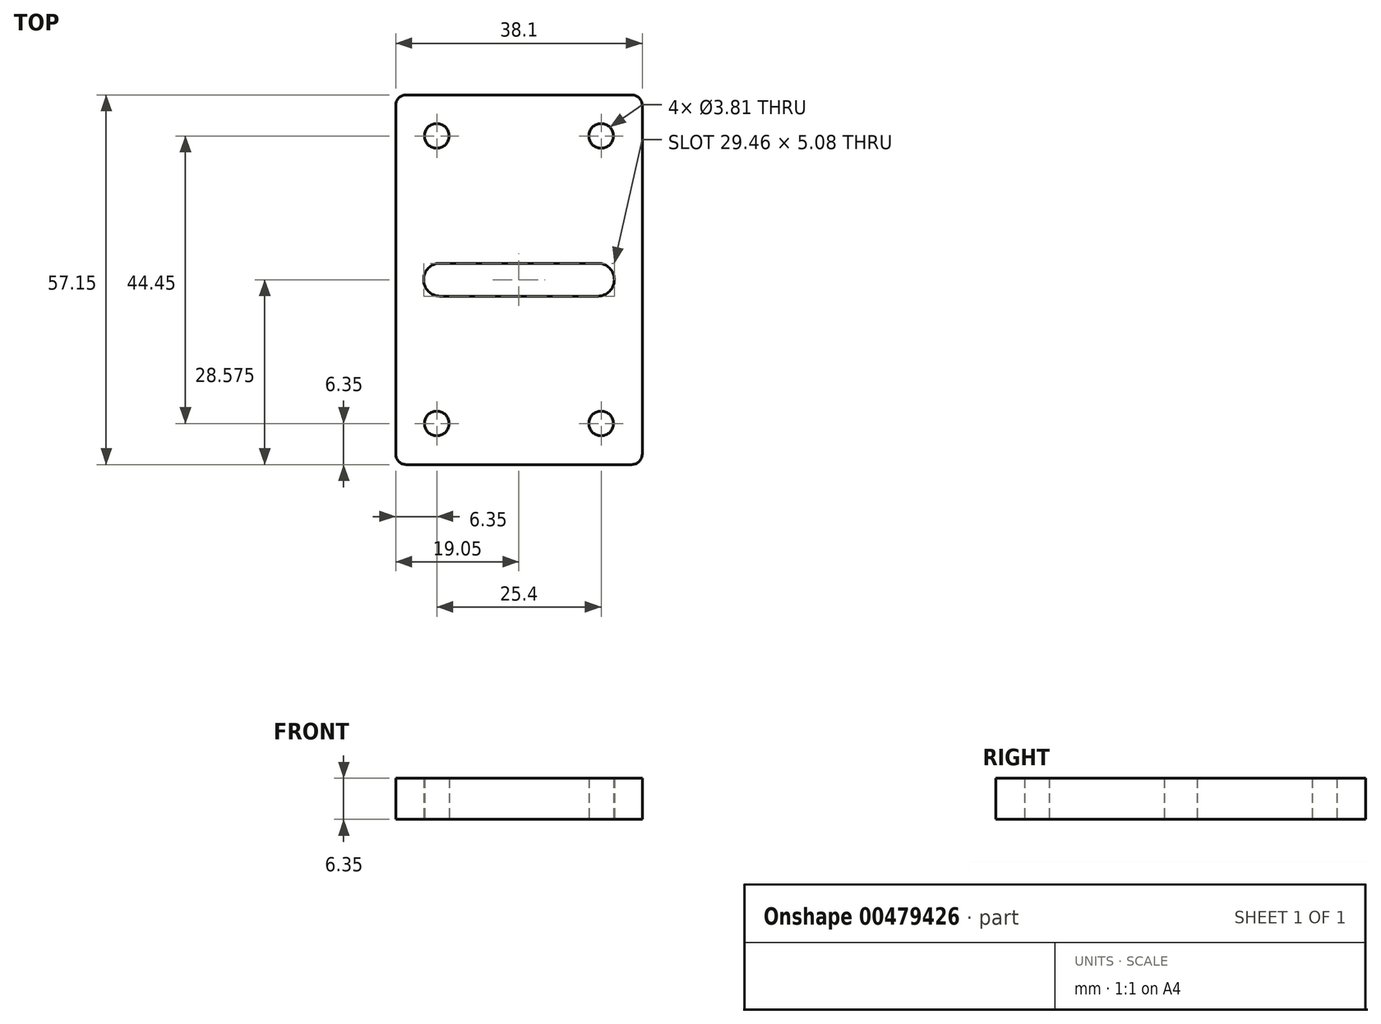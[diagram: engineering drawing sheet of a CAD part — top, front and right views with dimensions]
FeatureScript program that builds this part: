
annotation { "Feature Type Name" : "Feature", "Feature Type Description" : "" }
export const myFeature = defineFeature(function(context is Context, id is Id, definition is map)
    precondition{}
    {
        {
            var Q0;
            Q0=qCreatedBy(makeId("Top.planeOp"),FACE);
            var sketch = newSketch(context, id + "F0", { "sketchPlane" : qUnion([Q0])});
            skLineSegment(sketch, "E0.bottom", {"start": v(1.6, 0) * mm, "end": v(36.5, 0) * mm});
            skLineSegment(sketch, "E0.top", {"start": v(1.6, 57.15) * mm, "end": v(36.5, 57.15) * mm});
            skLineSegment(sketch, "E0.left", {"start": v(0, 1.6) * mm, "end": v(0, 55.55) * mm});
            skLineSegment(sketch, "E0.right", {"start": v(38.1, 1.6) * mm, "end": v(38.1, 55.55) * mm});
            skCircle(sketch, "E1", {"center": v(6.35, 50.8) * mm, "radius": 1.9 * mm});
            skCircle(sketch, "E2", {"center": v(31.75, 50.8) * mm, "radius": 1.9 * mm});
            skCircle(sketch, "E3", {"center": v(6.35, 6.35) * mm, "radius": 1.9 * mm});
            skCircle(sketch, "E4", {"center": v(31.75, 6.35) * mm, "radius": 1.9 * mm});
            skCircle(sketch, "E5", {"center": v(6.86, 28.58) * mm, "radius": 2.54 * mm});
            skCircle(sketch, "E6", {"center": v(31.24, 28.58) * mm, "radius": 2.54 * mm});
            skPoint(sketch, "E7.visualSharp", {"position": v(0, 57.15) * mm});
            skArc(sketch, "E7.filletArc", {"start": v(1.6, 57.15) * mm, "mid": v(0.47, 56.68) * mm, "end": v(0, 55.55) * mm});
            skPoint(sketch, "E8.visualSharp", {"position": v(38.1, 57.15) * mm});
            skArc(sketch, "E8.filletArc", {"start": v(38.1, 55.55) * mm, "mid": v(37.63, 56.68) * mm, "end": v(36.5, 57.15) * mm});
            skPoint(sketch, "E9.visualSharp", {"position": v(38.1, 0) * mm});
            skArc(sketch, "E9.filletArc", {"start": v(36.5, 0) * mm, "mid": v(37.63, 0.47) * mm, "end": v(38.1, 1.6) * mm});
            skPoint(sketch, "E10.visualSharp", {"position": v(0, 0) * mm});
            skArc(sketch, "E10.filletArc", {"start": v(0, 1.6) * mm, "mid": v(0.47, 0.47) * mm, "end": v(1.6, 0) * mm});
            skLineSegment(sketch, "E11", {"start": v(6.86, 31.12) * mm, "end": v(31.24, 31.12) * mm});
            skLineSegment(sketch, "E12", {"start": v(6.86, 26.04) * mm, "end": v(31.24, 26.04) * mm});
            skSolve(sketch);
        }
        {
            var Q0;
            Q0=makeQuery(id+"F0.imprint","IMPRINT",FACE,{"disambiguationData":[TD([[makeQuery(id+"F0.imprint","IMPRINT",EDGE,{"derivedFrom":sQuery(id+"F0.wireOp",EDGE,"E0.bottom")}),1.0]])]});
            extrude(context, id + "F1", {"entities" : qUnion([Q0]), "depth" : 6.35 * mm});
        }
    });
